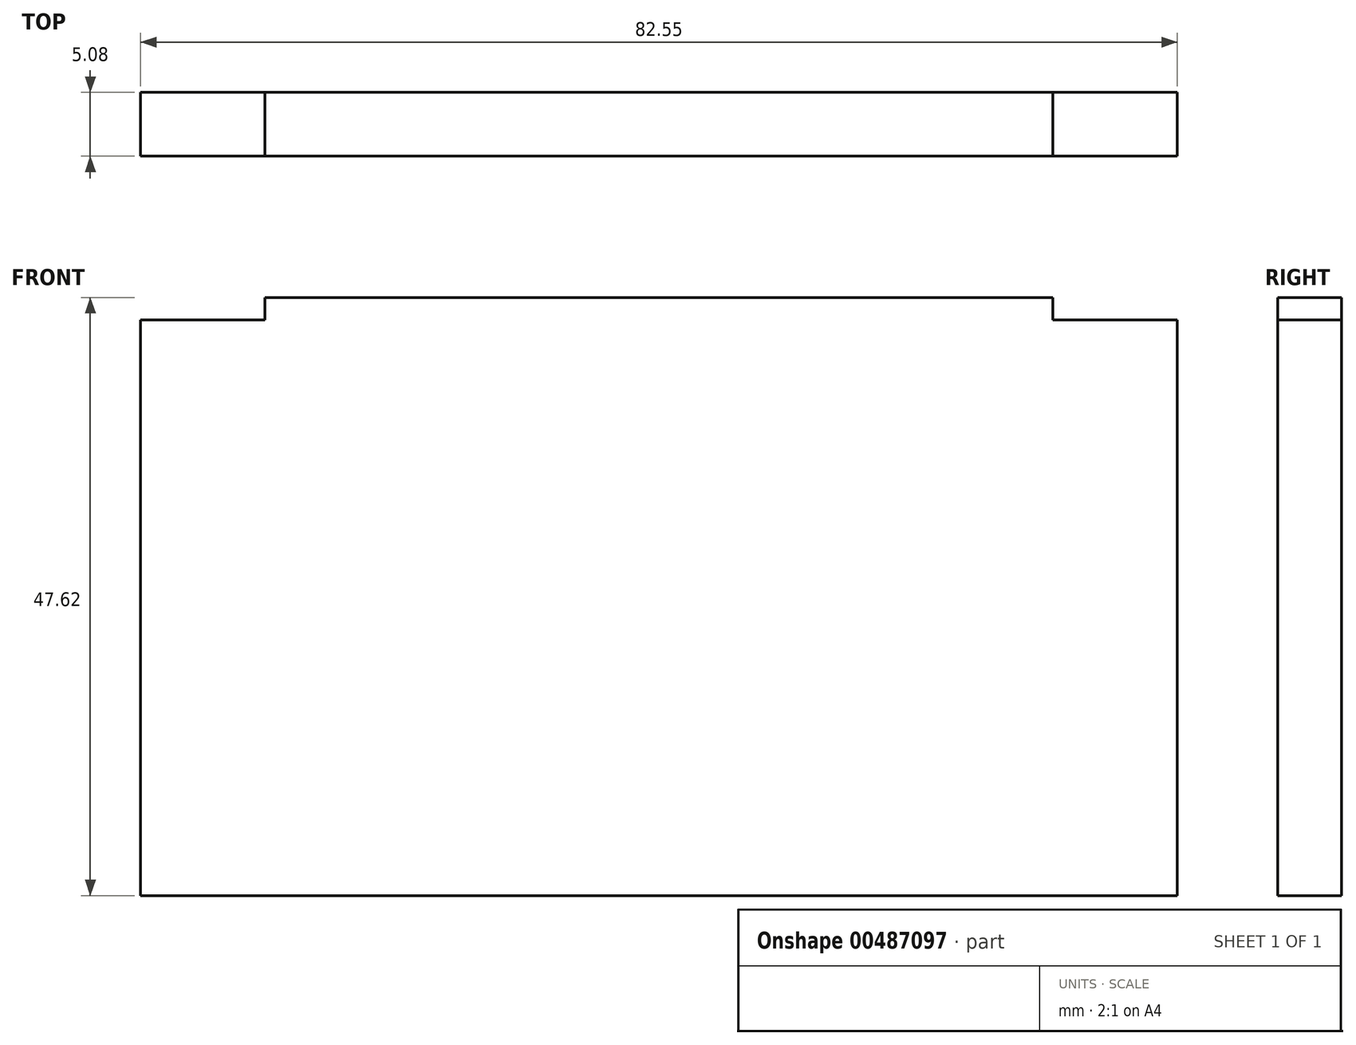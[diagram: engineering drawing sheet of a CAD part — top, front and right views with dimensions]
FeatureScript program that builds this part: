
annotation { "Feature Type Name" : "Feature", "Feature Type Description" : "" }
export const myFeature = defineFeature(function(context is Context, id is Id, definition is map)
    precondition{}
    {
        {
            var Q0;
            Q0=qCreatedBy(makeId("Front.planeOp"),FACE);
            var sketch = newSketch(context, id + "F0", { "sketchPlane" : qUnion([Q0])});
            skLineSegment(sketch, "E0.bottom", {"start": v(-17.13, 18.92) * mm, "end": v(45.61, 18.92) * mm});
            skLineSegment(sketch, "E0.top", {"start": v(-27.03, -28.7) * mm, "end": v(55.52, -28.7) * mm});
            skLineSegment(sketch, "E0.left", {"start": v(-27.03, 17.15) * mm, "end": v(-27.03, -28.7) * mm});
            skLineSegment(sketch, "E0.right", {"start": v(55.52, 17.15) * mm, "end": v(55.52, -28.7) * mm});
            skLineSegment(sketch, "E1.top", {"start": v(55.52, 17.15) * mm, "end": v(45.61, 17.15) * mm});
            skLineSegment(sketch, "E1.right", {"start": v(45.61, 18.92) * mm, "end": v(45.61, 17.15) * mm});
            skLineSegment(sketch, "E2.top", {"start": v(-27.03, 17.15) * mm, "end": v(-17.13, 17.15) * mm});
            skLineSegment(sketch, "E2.right", {"start": v(-17.13, 18.92) * mm, "end": v(-17.13, 17.15) * mm});
            skSolve(sketch);
        }
        {
            var Q0;
            Q0 = qSketchRegion(id + "F0", true);
            extrude(context, id + "F1", {"entities" : qUnion([Q0]), "depth" : 5.08 * mm});
        }
    });
